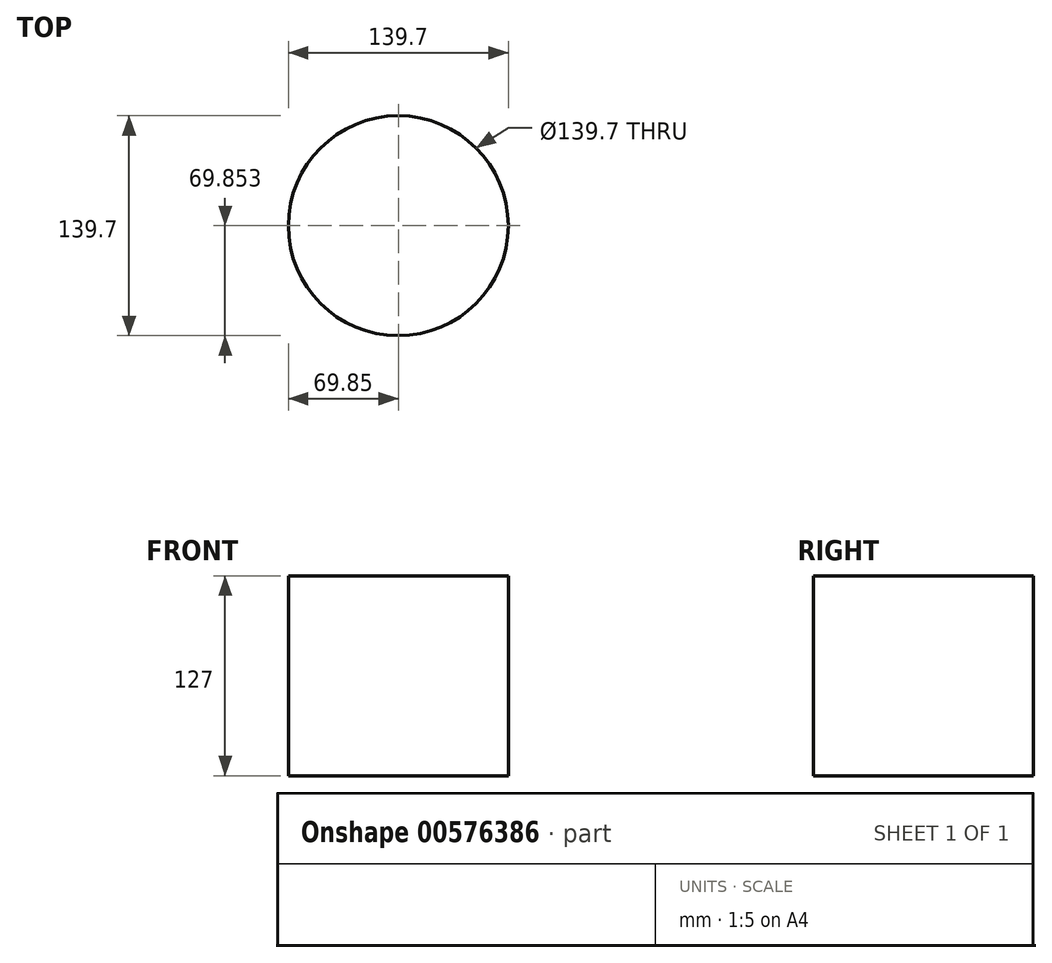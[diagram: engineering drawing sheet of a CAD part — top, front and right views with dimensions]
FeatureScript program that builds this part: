
annotation { "Feature Type Name" : "Feature", "Feature Type Description" : "" }
export const myFeature = defineFeature(function(context is Context, id is Id, definition is map)
    precondition{}
    {
        {
            var Q0;
            Q0=qCreatedBy(makeId("Top.planeOp"),FACE);
            var sketch = newSketch(context, id + "F0", { "sketchPlane" : qUnion([Q0])});
            skLineSegment(sketch, "E0", {"start": v(673.6, 0) * mm, "end": v(673.6, -140.43) * mm});
            skLineSegment(sketch, "E1", {"start": v(673.6, -140.43) * mm, "end": v(673.6, 0) * mm});
            skLineSegment(sketch, "E2", {"start": v(673.6, 0) * mm, "end": v(439.01, 0) * mm});
            skLineSegment(sketch, "E3", {"start": v(673.6, 0) * mm, "end": v(833.88, 55.7) * mm});
            skLineSegment(sketch, "E4.MirrorCS", {"start": v(673.6, 0) * mm, "end": v(586.51, 110.17) * mm});
            skLineSegment(sketch, "E5.MirrorCS", {"start": v(673.6, 0) * mm, "end": v(489.56, -145.46) * mm});
            skLineSegment(sketch, "E6.MirrorCS", {"start": v(586.51, 110.17) * mm, "end": v(673.6, 0) * mm});
            skCircle(sketch, "E7.cCircle", {"center": v(673.6, 0) * mm, "radius": 164 * mm, "construction": true});
            skLineSegment(sketch, "E7.0", {"start": v(1001.52, 6.27) * mm, "end": v(515.06, -287.13) * mm});
            skLineSegment(sketch, "E7.1", {"start": v(515.06, -287.13) * mm, "end": v(504.2, 280.86) * mm});
            skLineSegment(sketch, "E7.2", {"start": v(504.2, 280.86) * mm, "end": v(1001.52, 6.27) * mm});
            skPoint(sketch, "E7.0.midPoint", {"position": v(758.3, -140.43) * mm});
            skCircle(sketch, "E8", {"center": v(673.6, 0) * mm, "radius": 328 * mm});
            skLineSegment(sketch, "E9.bottom", {"start": v(439.01, 0) * mm, "end": v(673.6, 0) * mm});
            skLineSegment(sketch, "E9.top", {"start": v(439.01, -70.21) * mm, "end": v(673.6, -70.21) * mm});
            skLineSegment(sketch, "E9.left", {"start": v(439.01, 0) * mm, "end": v(439.01, -70.21) * mm});
            skLineSegment(sketch, "E9.right", {"start": v(673.6, 0) * mm, "end": v(673.6, -70.21) * mm});
            skLineSegment(sketch, "E10.bottom", {"start": v(673.6, 0) * mm, "end": v(758.3, 0) * mm});
            skLineSegment(sketch, "E10.top", {"start": v(673.6, -316.87) * mm, "end": v(758.3, -316.87) * mm});
            skLineSegment(sketch, "E10.left", {"start": v(673.6, 0) * mm, "end": v(673.6, -316.87) * mm});
            skLineSegment(sketch, "E10.right", {"start": v(758.3, 0) * mm, "end": v(758.3, -316.87) * mm});
            skLineSegment(sketch, "E11.top", {"start": v(673.6, 316.87) * mm, "end": v(758.3, 316.87) * mm});
            skLineSegment(sketch, "E11.left", {"start": v(673.6, 0) * mm, "end": v(673.6, 316.87) * mm});
            skLineSegment(sketch, "E11.right", {"start": v(758.3, 0) * mm, "end": v(758.3, 316.87) * mm});
            skCircle(sketch, "E12.cCircle", {"center": v(673.6, 0) * mm, "radius": 286.7 * mm, "construction": true});
            skLineSegment(sketch, "E12.0", {"start": v(320.93, 34.95) * mm, "end": v(597.85, 346.2) * mm});
            skLineSegment(sketch, "E12.1", {"start": v(597.85, 346.2) * mm, "end": v(979.45, 179.01) * mm});
            skLineSegment(sketch, "E12.2", {"start": v(979.45, 179.01) * mm, "end": v(938.36, -235.57) * mm});
            skLineSegment(sketch, "E12.3", {"start": v(938.36, -235.57) * mm, "end": v(531.37, -324.6) * mm});
            skLineSegment(sketch, "E12.4", {"start": v(531.37, -324.6) * mm, "end": v(320.93, 34.95) * mm});
            skPoint(sketch, "E12.0.midPoint", {"position": v(459.39, 190.58) * mm});
            skCircle(sketch, "E13", {"center": v(0, 0.3) * mm, "radius": 69.85 * mm});
            skSolve(sketch);
        }
        {
            var Q0;
            Q0=sQuery(id+"F0.wireOp",EDGE,"E13");
            extrude(context, id + "F1", {"bodyType" : ToolBodyType.SURFACE, "operationType" : NewBodyOperationType.ADD, "surfaceEntities" : qUnion([Q0]), "oppositeDirection" : true, "depth" : 127 * mm, "offsetDistance" : 25.4 * mm});
        }
    });
